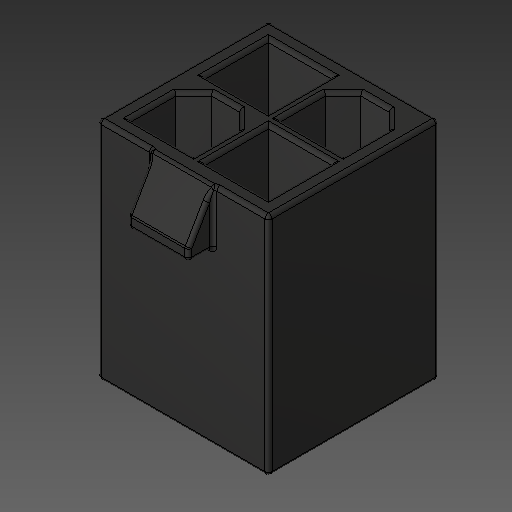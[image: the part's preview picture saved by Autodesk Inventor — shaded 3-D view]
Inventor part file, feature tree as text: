
AUTODESK INVENTOR PART (.ipt)
format: ipt  version: 2018.2 (Build 222227000, 227)  size: 173,568 bytes
history: native  units: mm
features: other x1, fillet x1
ambient origin geometry x8: Origin, YZ Plane, XZ Plane, XY Plane, X Axis, Y Axis, Z Axis, Center Point
bodies: Body1 (feature_tree)
feature tree (2):
  other  "ソリッド1"
  fillet  "Fillet1"  [1 undecoded]
note: 1 required parameter value undecoded (feature->parameter linkage not recoverable at this tier; creation-order binding heuristic only, values carry confidence <= 0.55)
